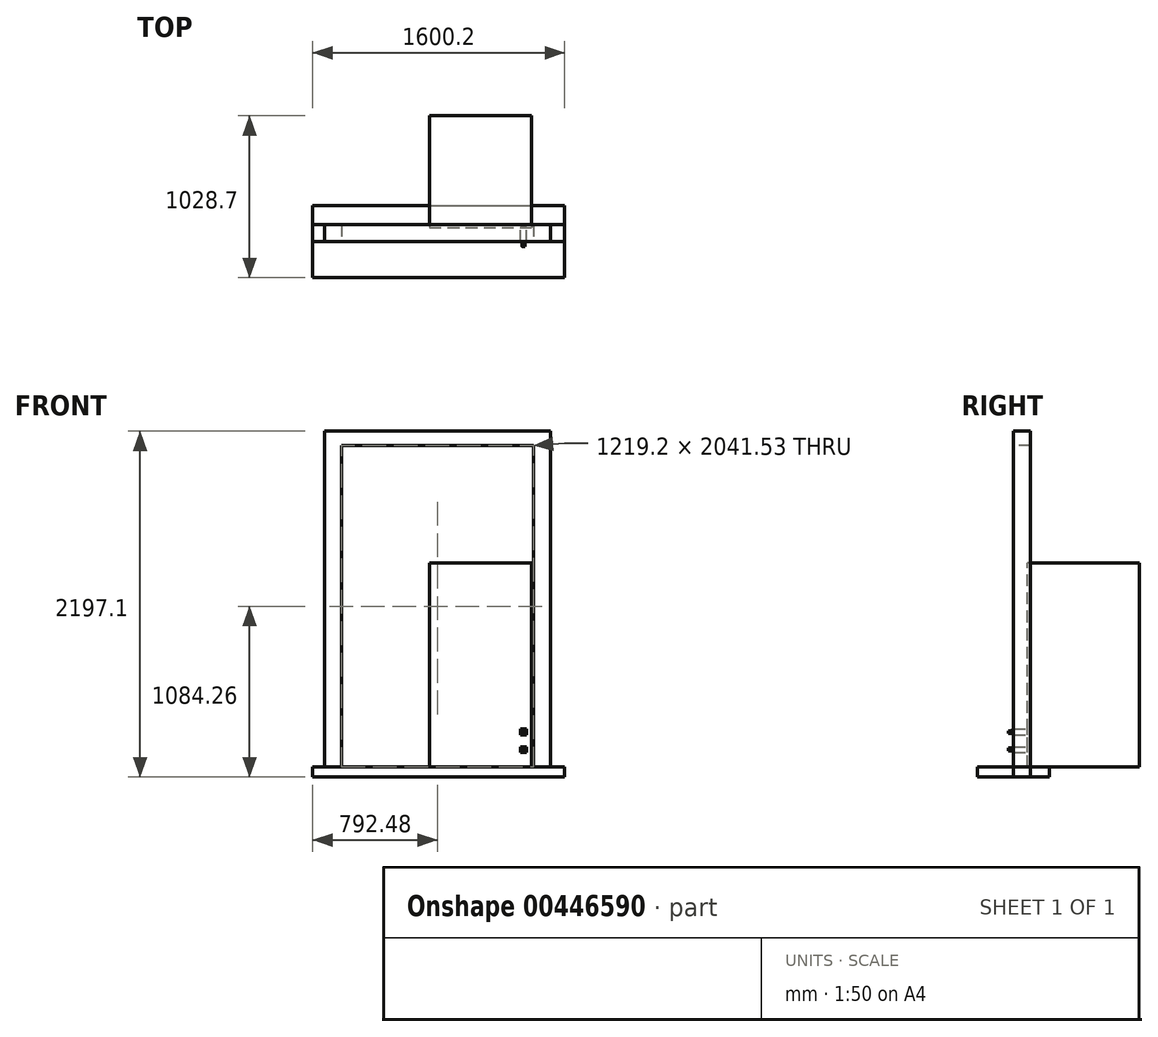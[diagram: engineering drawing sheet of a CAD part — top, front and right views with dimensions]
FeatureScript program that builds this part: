
annotation { "Feature Type Name" : "Feature", "Feature Type Description" : "" }
export const myFeature = defineFeature(function(context is Context, id is Id, definition is map)
    precondition{}
    {
        {
            var Q0;
            Q0=qCreatedBy(makeId("Front.planeOp"),FACE);
            var sketch = newSketch(context, id + "F0", { "sketchPlane" : qUnion([Q0])});
            skLineSegment(sketch, "E0.bottom", {"start": v(0, 0) * mm, "end": v(1219.2, 0) * mm});
            skLineSegment(sketch, "E0.top", {"start": v(0, 2041.53) * mm, "end": v(1219.2, 2041.53) * mm});
            skLineSegment(sketch, "E0.left", {"start": v(0, 0) * mm, "end": v(0, 2041.53) * mm});
            skLineSegment(sketch, "E0.right", {"start": v(1219.2, 0) * mm, "end": v(1219.2, 2041.53) * mm});
            skLineSegment(sketch, "E1.bottom", {"start": v(-182.88, 0) * mm, "end": v(1417.32, 0) * mm});
            skLineSegment(sketch, "E1.top", {"start": v(-182.88, -63.5) * mm, "end": v(1417.32, -63.5) * mm});
            skLineSegment(sketch, "E1.left", {"start": v(-182.88, 0) * mm, "end": v(-182.88, -63.5) * mm});
            skLineSegment(sketch, "E1.right", {"start": v(1417.32, 0) * mm, "end": v(1417.32, -63.5) * mm});
            skLineSegment(sketch, "E2", {"start": v(-106.68, 0) * mm, "end": v(-106.68, 2133.6) * mm});
            skLineSegment(sketch, "E3", {"start": v(-106.68, 2133.6) * mm, "end": v(1328.42, 2133.6) * mm});
            skLineSegment(sketch, "E4", {"start": v(1328.42, 2133.6) * mm, "end": v(1328.42, 0) * mm});
            skLineSegment(sketch, "E5", {"start": v(1206.5, 0) * mm, "end": v(1206.5, 1295.4) * mm});
            skLineSegment(sketch, "E6", {"start": v(1206.5, 1295.4) * mm, "end": v(558.8, 1295.4) * mm});
            skLineSegment(sketch, "E7", {"start": v(558.8, 1295.4) * mm, "end": v(558.8, 0) * mm});
            skLineSegment(sketch, "E8.bottom", {"start": v(1136.65, 203.2) * mm, "end": v(1174.75, 203.2) * mm});
            skLineSegment(sketch, "E8.top", {"start": v(1136.65, 241.3) * mm, "end": v(1174.75, 241.3) * mm});
            skLineSegment(sketch, "E8.left", {"start": v(1136.65, 203.2) * mm, "end": v(1136.65, 241.3) * mm});
            skLineSegment(sketch, "E8.right", {"start": v(1174.75, 203.2) * mm, "end": v(1174.75, 241.3) * mm});
            skPoint(sketch, "E8.middle", {"position": v(1155.7, 222.25) * mm});
            skLineSegment(sketch, "E9.bottom", {"start": v(1174.75, 92.08) * mm, "end": v(1136.65, 92.08) * mm});
            skLineSegment(sketch, "E9.top", {"start": v(1174.75, 130.18) * mm, "end": v(1136.65, 130.18) * mm});
            skLineSegment(sketch, "E9.left", {"start": v(1174.75, 92.08) * mm, "end": v(1174.75, 130.18) * mm});
            skLineSegment(sketch, "E9.right", {"start": v(1136.65, 92.08) * mm, "end": v(1136.65, 130.18) * mm});
            skPoint(sketch, "E9.middle", {"position": v(1155.7, 111.13) * mm});
            skSolve(sketch);
        }
        {
            var Q0;
            Q0=makeQuery(id+"F0.imprint","IMPRINT",FACE,{"disambiguationData":[TD([[makeQuery(id+"F0.imprint","IMPRINT",EDGE,{"derivedFrom":sQuery(id+"F0.wireOp",EDGE,"E1.top")}),1.0]])]});
            extrude(context, id + "F1", {"entities" : qUnion([Q0]), "endBound" : BoundingType.SYMMETRIC, "depth" : 457.2 * mm});
        }
        {
            var Q0;
            Q0 = qSketchRegion(id + "F0", true);
            extrude(context, id + "F2", {"entities" : qUnion([Q0]), "oppositeDirection" : true, "depth" : 107.95 * mm});
        }
        {
            var Q0;
            Q0=makeQuery(id+"F2.opExtrude","CAP_FACE",FACE,{"disambiguationData":[OSD([sQuery(id+"F0.wireOp",EDGE,"E0.top"),sQuery(id+"F0.wireOp",EDGE,"E0.left"),sQuery(id+"F0.wireOp",EDGE,"E0.right"),sQuery(id+"F0.wireOp",EDGE,"E1.bottom"),sQuery(id+"F0.wireOp",EDGE,"E1.top"),sQuery(id+"F0.wireOp",EDGE,"E1.left"),sQuery(id+"F0.wireOp",EDGE,"E1.right"),sQuery(id+"F0.wireOp",EDGE,"E2"),sQuery(id+"F0.wireOp",EDGE,"E3"),sQuery(id+"F0.wireOp",EDGE,"E4")])],"isStart":true});
            cPlane(context, id + "F3", {"entities" : qUnion([Q0]), "cplaneType" : CPlaneType.OFFSET, "offset" : 88.9 * mm, "oppositeDirection" : true, "width" : 152.4 * mm, "height" : 152.4 * mm});
        }
        {
            var Q0;
            Q0=qCreatedBy(id+"F3.planeOp",FACE);
            var sketch = newSketch(context, id + "F4", { "sketchPlane" : qUnion([Q0])});
            skLineSegment(sketch, "E10.bottom", {"start": v(558.8, 0) * mm, "end": v(1206.5, 0) * mm});
            skLineSegment(sketch, "E10.top", {"start": v(558.8, 1295.4) * mm, "end": v(1206.5, 1295.4) * mm});
            skLineSegment(sketch, "E10.left", {"start": v(558.8, 0) * mm, "end": v(558.8, 1295.4) * mm});
            skLineSegment(sketch, "E10.right", {"start": v(1206.5, 0) * mm, "end": v(1206.5, 1295.4) * mm});
            skSolve(sketch);
        }
        {
            var Q0;
            Q0=makeQuery(id+"F4.imprint","IMPRINT",FACE,{"disambiguationData":[TD([[makeQuery(id+"F4.imprint","IMPRINT",EDGE,{"derivedFrom":sQuery(id+"F4.wireOp",EDGE,"E10.bottom")}),1.0]])]});
            extrude(context, id + "F5", {"entities" : qUnion([Q0]), "oppositeDirection" : true, "depth" : 711.2 * mm});
        }
        {
            var Q0;
            Q0=makeQuery(id+"F5.opExtrude","CAP_FACE",FACE,{"disambiguationData":[OSD([sQuery(id+"F4.wireOp",EDGE,"E10.bottom"),sQuery(id+"F4.wireOp",EDGE,"E10.top"),sQuery(id+"F4.wireOp",EDGE,"E10.left"),sQuery(id+"F4.wireOp",EDGE,"E10.right")])],"isStart":true});
            var sketch = newSketch(context, id + "F6", { "sketchPlane" : qUnion([Q0])});
            skLineSegment(sketch, "E11.bottom", {"start": v(1174.75, 203.2) * mm, "end": v(1136.65, 203.2) * mm});
            skLineSegment(sketch, "E11.top", {"start": v(1174.75, 241.3) * mm, "end": v(1136.65, 241.3) * mm});
            skLineSegment(sketch, "E11.left", {"start": v(1174.75, 203.2) * mm, "end": v(1174.75, 241.3) * mm});
            skLineSegment(sketch, "E11.right", {"start": v(1136.65, 203.2) * mm, "end": v(1136.65, 241.3) * mm});
            skPoint(sketch, "E11.middle", {"position": v(1155.7, 222.25) * mm});
            skLineSegment(sketch, "E12.bottom", {"start": v(1136.65, 93.14) * mm, "end": v(1174.75, 93.14) * mm});
            skLineSegment(sketch, "E12.top", {"start": v(1136.65, 129.1) * mm, "end": v(1174.75, 129.1) * mm});
            skLineSegment(sketch, "E12.left", {"start": v(1136.65, 93.14) * mm, "end": v(1136.65, 131.24) * mm});
            skLineSegment(sketch, "E12.right", {"start": v(1174.75, 93.14) * mm, "end": v(1174.75, 129.1) * mm});
            skPoint(sketch, "E12.middle", {"position": v(1155.7, 111.13) * mm});
            skPoint(sketch, "E12.middle.positionSnap0", {"position": v(1155.7, 203.2) * mm});
            skPoint(sketch, "E12.centerSnap0", {"position": v(1155.7, 203.2) * mm});
            skSolve(sketch);
        }
        {
            var Q0;
            Q0=makeQuery(id+"F6.imprint","IMPRINT",FACE,{"disambiguationData":[TD([[makeQuery(id+"F6.imprint","IMPRINT",EDGE,{"derivedFrom":sQuery(id+"F6.wireOp",EDGE,"E11.bottom")}),-1.0]])]});
            extrude(context, id + "F7", {"entities" : qUnion([Q0]), "operationType" : NewBodyOperationType.ADD, "depth" : 95.25 * mm});
        }
        {
            var Q0;
            Q0 = qSketchRegion(id + "F6", true);
            extrude(context, id + "F8", {"entities" : qUnion([Q0]), "depth" : 95.25 * mm});
        }
        {
            var Q0;
            Q0=makeQuery(id+"F8.opExtrude","CAP_FACE",FACE,{"disambiguationData":[OSD([sQuery(id+"F6.wireOp",EDGE,"E12.bottom"),sQuery(id+"F6.wireOp",EDGE,"E12.top"),sQuery(id+"F6.wireOp",EDGE,"E12.left"),sQuery(id+"F6.wireOp",EDGE,"E12.right")])],"isStart":false});
            var sketch = newSketch(context, id + "F9", { "sketchPlane" : qUnion([Q0])});
            skCircle(sketch, "E13", {"center": v(1156.39, 111.13) * mm, "radius": 9.53 * mm});
            skPoint(sketch, "E13.centerSnap0", {"position": v(1136.65, 111.13) * mm});
            skSolve(sketch);
        }
        {
            var Q0;
            Q0 = qSketchRegion(id + "F9", true);
            extrude(context, id + "F10", {"entities" : qUnion([Q0]), "operationType" : NewBodyOperationType.ADD, "depth" : 25.4 * mm});
        }
        {
            var Q0;
            Q0=makeQuery(id+"F7.opExtrude","CAP_FACE",FACE,{"disambiguationData":[OSD([sQuery(id+"F6.wireOp",EDGE,"E11.bottom"),sQuery(id+"F6.wireOp",EDGE,"E11.top"),sQuery(id+"F6.wireOp",EDGE,"E11.left"),sQuery(id+"F6.wireOp",EDGE,"E11.right")])],"isStart":false});
            var sketch = newSketch(context, id + "F11", { "sketchPlane" : qUnion([Q0])});
            skCircle(sketch, "E14", {"center": v(1155.7, 222.25) * mm, "radius": 9.04 * mm});
            skPoint(sketch, "E14.centerSnap0", {"position": v(1136.65, 222.25) * mm});
            skSolve(sketch);
        }
        {
            var Q0;
            Q0 = qSketchRegion(id + "F11", true);
            extrude(context, id + "F12", {"entities" : qUnion([Q0]), "depth" : 25.4 * mm});
        }
    });
